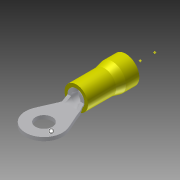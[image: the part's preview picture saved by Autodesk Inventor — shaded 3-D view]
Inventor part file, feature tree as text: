
AUTODESK INVENTOR PART (.ipt)
format: ipt  version: 2011 (Build 150239000, 239)  size: 176,128 bytes
history: native  units: mm
features: other x4, plane x2, imported_body x1, sketch x1
ambient origin geometry x8: Origin, YZ Plane, XZ Plane, XY Plane, X Axis, Y Axis, Z Axis, Center Point
bodies: Solid1 (feature_tree)
feature tree (8):
  imported_body  "Base1"
  sketch  "Sketch1"  dims[d0=3.175mm d1=6.35mm d2=0.0mm]
  other  "Work Point2"
  other  "Work Point3"
  plane  "Work Plane1"
  other  "Work Axis1"
  plane  "Work Plane2"
  other  "Work Axis2"
